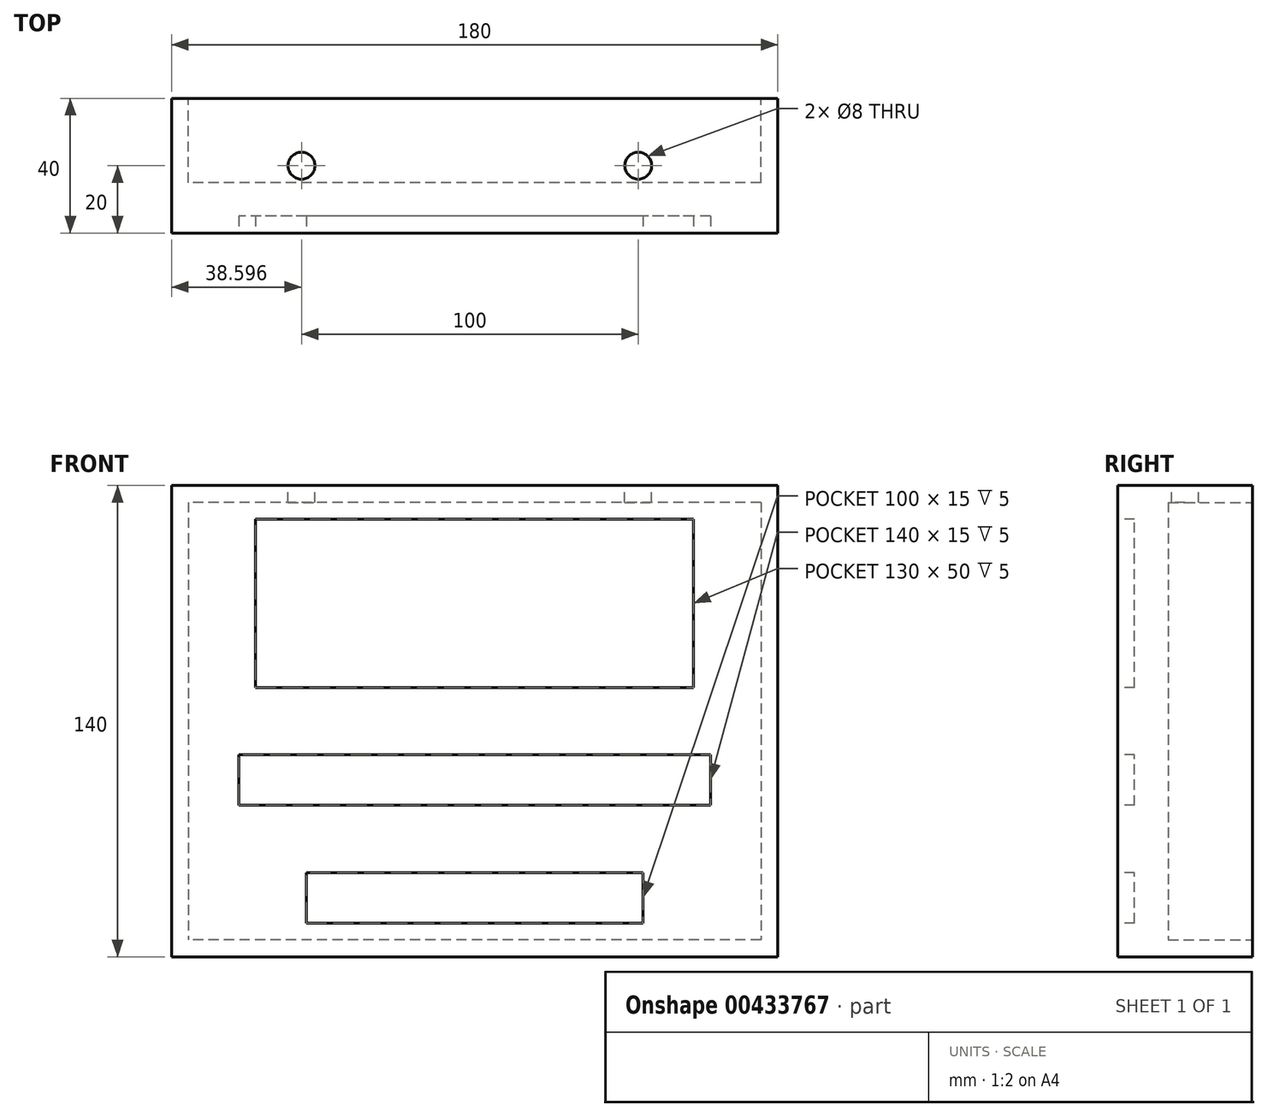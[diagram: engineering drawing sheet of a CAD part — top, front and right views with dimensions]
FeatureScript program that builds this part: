
annotation { "Feature Type Name" : "Feature", "Feature Type Description" : "" }
export const myFeature = defineFeature(function(context is Context, id is Id, definition is map)
    precondition{}
    {
        {
            var Q0;
            Q0=qCreatedBy(makeId("Front.planeOp"),FACE);
            var sketch = newSketch(context, id + "F0", { "sketchPlane" : qUnion([Q0])});
            skLineSegment(sketch, "E0.bottom", {"start": v(90, -70) * mm, "end": v(-90, -70) * mm});
            skLineSegment(sketch, "E0.top", {"start": v(90, 70) * mm, "end": v(-90, 70) * mm});
            skLineSegment(sketch, "E0.left", {"start": v(90, -70) * mm, "end": v(90, 70) * mm});
            skLineSegment(sketch, "E0.right", {"start": v(-90, -70) * mm, "end": v(-90, 70) * mm});
            skPoint(sketch, "E0.middle", {"position": v(0, 0) * mm});
            skSolve(sketch);
        }
        {
            var Q0;
            Q0=makeQuery(id+"F0.imprint","IMPRINT",FACE,{"disambiguationData":[TD([[makeQuery(id+"F0.imprint","IMPRINT",EDGE,{"derivedFrom":sQuery(id+"F0.wireOp",EDGE,"E0.bottom")}),-1.0]])]});
            extrude(context, id + "F1", {"entities" : qUnion([Q0]), "depth" : 40 * mm});
        }
        {
            var Q0;
            Q0=makeQuery(id+"F1.opExtrude","CAP_FACE",FACE,{"disambiguationData":[OSD([sQuery(id+"F0.wireOp",EDGE,"E0.bottom"),sQuery(id+"F0.wireOp",EDGE,"E0.top"),sQuery(id+"F0.wireOp",EDGE,"E0.left"),sQuery(id+"F0.wireOp",EDGE,"E0.right")])],"isStart":false});
            var sketch = newSketch(context, id + "F2", { "sketchPlane" : qUnion([Q0])});
            skLineSegment(sketch, "E1.bottom", {"start": v(50, -60) * mm, "end": v(-50, -60) * mm});
            skLineSegment(sketch, "E1.top", {"start": v(50, -45) * mm, "end": v(-50, -45) * mm});
            skLineSegment(sketch, "E1.left", {"start": v(50, -60) * mm, "end": v(50, -45) * mm});
            skLineSegment(sketch, "E1.right", {"start": v(-50, -60) * mm, "end": v(-50, -45) * mm});
            skPoint(sketch, "E1.middle", {"position": v(0, -52.5) * mm});
            skLineSegment(sketch, "E2.bottom", {"start": v(70, -25) * mm, "end": v(-70, -25) * mm});
            skLineSegment(sketch, "E2.top", {"start": v(70, -10) * mm, "end": v(-70, -10) * mm});
            skLineSegment(sketch, "E2.left", {"start": v(70, -25) * mm, "end": v(70, -10) * mm});
            skLineSegment(sketch, "E2.right", {"start": v(-70, -25) * mm, "end": v(-70, -10) * mm});
            skPoint(sketch, "E2.middle", {"position": v(0, -17.5) * mm});
            skLineSegment(sketch, "E3.bottom", {"start": v(65, 10) * mm, "end": v(-65, 10) * mm});
            skLineSegment(sketch, "E3.top", {"start": v(65, 60) * mm, "end": v(-65, 60) * mm});
            skLineSegment(sketch, "E3.left", {"start": v(65, 10) * mm, "end": v(65, 60) * mm});
            skLineSegment(sketch, "E3.right", {"start": v(-65, 10) * mm, "end": v(-65, 60) * mm});
            skPoint(sketch, "E3.middle", {"position": v(0, 35) * mm});
            skSolve(sketch);
        }
        {
            var Q0;
            Q0=makeQuery(id+"F2.imprint","IMPRINT",FACE,{"disambiguationData":[TD([[makeQuery(id+"F2.imprint","IMPRINT",EDGE,{"derivedFrom":sQuery(id+"F2.wireOp",EDGE,"E3.bottom")}),-1.0]])]});
            var Q1;
            Q1=makeQuery(id+"F2.imprint","IMPRINT",FACE,{"disambiguationData":[TD([[makeQuery(id+"F2.imprint","IMPRINT",EDGE,{"derivedFrom":sQuery(id+"F2.wireOp",EDGE,"E2.bottom")}),-1.0]])]});
            var Q2;
            Q2=makeQuery(id+"F2.imprint","IMPRINT",FACE,{"disambiguationData":[TD([[makeQuery(id+"F2.imprint","IMPRINT",EDGE,{"derivedFrom":sQuery(id+"F2.wireOp",EDGE,"E1.bottom")}),-1.0]])]});
            extrude(context, id + "F3", {"entities" : qUnion([Q0, Q1, Q2]), "operationType" : NewBodyOperationType.REMOVE, "oppositeDirection" : true, "depth" : 5 * mm});
        }
        {
            var Q0;
            Q0=makeQuery(id+"F1.opExtrude","CAP_FACE",FACE,{"disambiguationData":[OSD([sQuery(id+"F0.wireOp",EDGE,"E0.bottom"),sQuery(id+"F0.wireOp",EDGE,"E0.top"),sQuery(id+"F0.wireOp",EDGE,"E0.left"),sQuery(id+"F0.wireOp",EDGE,"E0.right")])],"isStart":true});
            var sketch = newSketch(context, id + "F4", { "sketchPlane" : qUnion([Q0])});
            skLineSegment(sketch, "E4.bottom", {"start": v(-85, 65) * mm, "end": v(85, 65) * mm});
            skLineSegment(sketch, "E4.top", {"start": v(-85, -65) * mm, "end": v(85, -65) * mm});
            skLineSegment(sketch, "E4.left", {"start": v(-85, 65) * mm, "end": v(-85, -65) * mm});
            skLineSegment(sketch, "E4.right", {"start": v(85, 65) * mm, "end": v(85, -65) * mm});
            skPoint(sketch, "E4.middle", {"position": v(0, 0) * mm});
            skSolve(sketch);
        }
        {
            var Q0;
            Q0=makeQuery(id+"F4.imprint","IMPRINT",FACE,{"disambiguationData":[TD([[makeQuery(id+"F4.imprint","IMPRINT",EDGE,{"derivedFrom":sQuery(id+"F4.wireOp",EDGE,"E4.bottom")}),-1.0]])]});
            extrude(context, id + "F5", {"entities" : qUnion([Q0]), "operationType" : NewBodyOperationType.REMOVE, "oppositeDirection" : true, "depth" : 25 * mm});
        }
        {
            var Q0;
            Q0=makeQuery(id+"F1.opExtrude","SWEPT_FACE",FACE,{"disambiguationData":[OSD([sQuery(id+"F0.wireOp",EDGE,"E0.top")])]});
            var sketch = newSketch(context, id + "F6", { "sketchPlane" : qUnion([Q0])});
            skCircle(sketch, "E5", {"center": v(48.6, -20) * mm, "radius": 4 * mm});
            skCircle(sketch, "E6", {"center": v(-51.4, -20) * mm, "radius": 4 * mm});
            skSolve(sketch);
        }
        {
            var Q0;
            Q0 = qSketchRegion(id + "F6", true);
            extrude(context, id + "F7", {"entities" : qUnion([Q0]), "operationType" : NewBodyOperationType.REMOVE, "oppositeDirection" : true, "depth" : 25 * mm});
        }
    });
